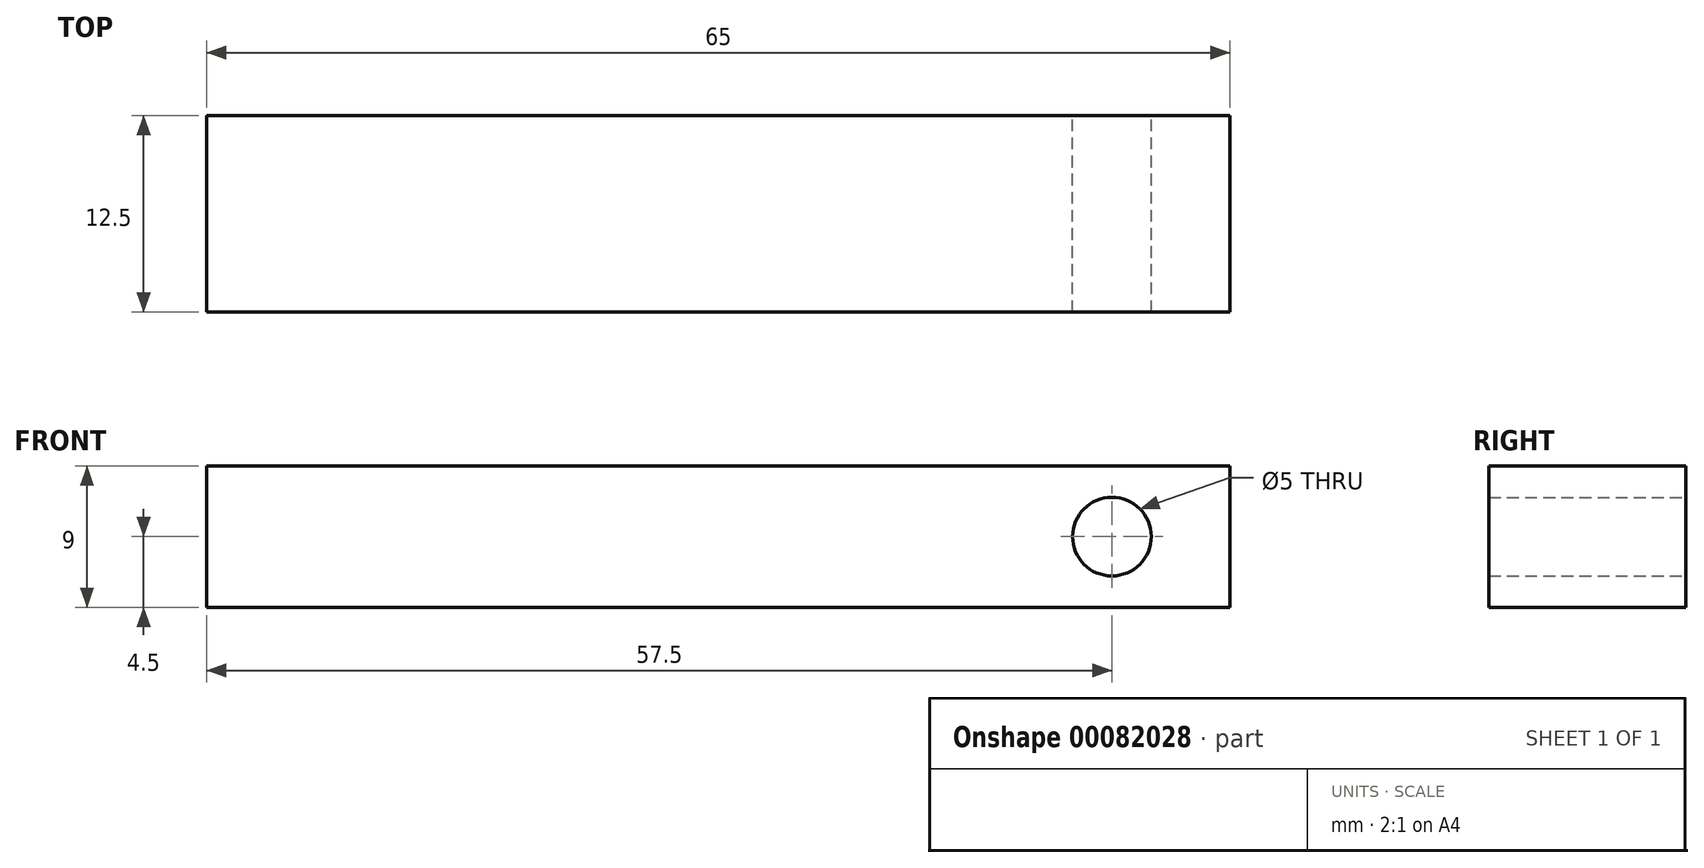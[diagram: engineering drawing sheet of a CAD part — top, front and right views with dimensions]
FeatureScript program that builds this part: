
annotation { "Feature Type Name" : "Feature", "Feature Type Description" : "" }
export const myFeature = defineFeature(function(context is Context, id is Id, definition is map)
    precondition{}
    {
        {
            var Q0;
            Q0=qCreatedBy(makeId("Front.planeOp"),FACE);
            var sketch = newSketch(context, id + "F0", { "sketchPlane" : qUnion([Q0])});
            skLineSegment(sketch, "E0.bottom", {"start": v(0, 0) * mm, "end": v(-65, 0) * mm});
            skLineSegment(sketch, "E0.top", {"start": v(0, 9) * mm, "end": v(-65, 9) * mm});
            skLineSegment(sketch, "E0.left", {"start": v(0, 0) * mm, "end": v(0, 9) * mm});
            skLineSegment(sketch, "E0.right", {"start": v(-65, 0) * mm, "end": v(-65, 9) * mm});
            skLineSegment(sketch, "E1", {"start": v(-32.5, 9) * mm, "end": v(-32.5, 0) * mm, "construction": true});
            skCircle(sketch, "E2", {"center": v(-57.5, 4.5) * mm, "radius": 2.5 * mm});
            skLineSegment(sketch, "E3", {"start": v(-65, 4.5) * mm, "end": v(0, 4.5) * mm, "construction": true});
            skCircle(sketch, "E4.MirrorC", {"center": v(-7.5, 4.5) * mm, "radius": 2.5 * mm});
            skSolve(sketch);
        }
        {
            var Q0;
            Q0=makeQuery(id+"F0.imprint","IMPRINT",FACE,{"disambiguationData":[TD([[makeQuery(id+"F0.imprint","IMPRINT",EDGE,{"derivedFrom":sQuery(id+"F0.wireOp",EDGE,"E0.bottom")}),-1.0]])]});
            extrude(context, id + "F1", {"entities" : qUnion([Q0]), "depth" : 9 * mm});
        }
        {
            var Q0;
            Q0=makeQuery(id+"F0.imprint","IMPRINT",FACE,{"disambiguationData":[TD([[makeQuery(id+"F0.imprint","IMPRINT",EDGE,{"derivedFrom":sQuery(id+"F0.wireOp",EDGE,"E2")}),1.0]])]});
            var Q1;
            Q1=makeQuery(id+"F0.imprint","IMPRINT",FACE,{"disambiguationData":[TD([[makeQuery(id+"F0.imprint","IMPRINT",EDGE,{"derivedFrom":sQuery(id+"F0.wireOp",EDGE,"E4.MirrorC")}),-1.0]])]});
            extrude(context, id + "F2", {"entities" : qUnion([Q0, Q1]), "operationType" : NewBodyOperationType.ADD, "depth" : 12.5 * mm});
        }
    });
